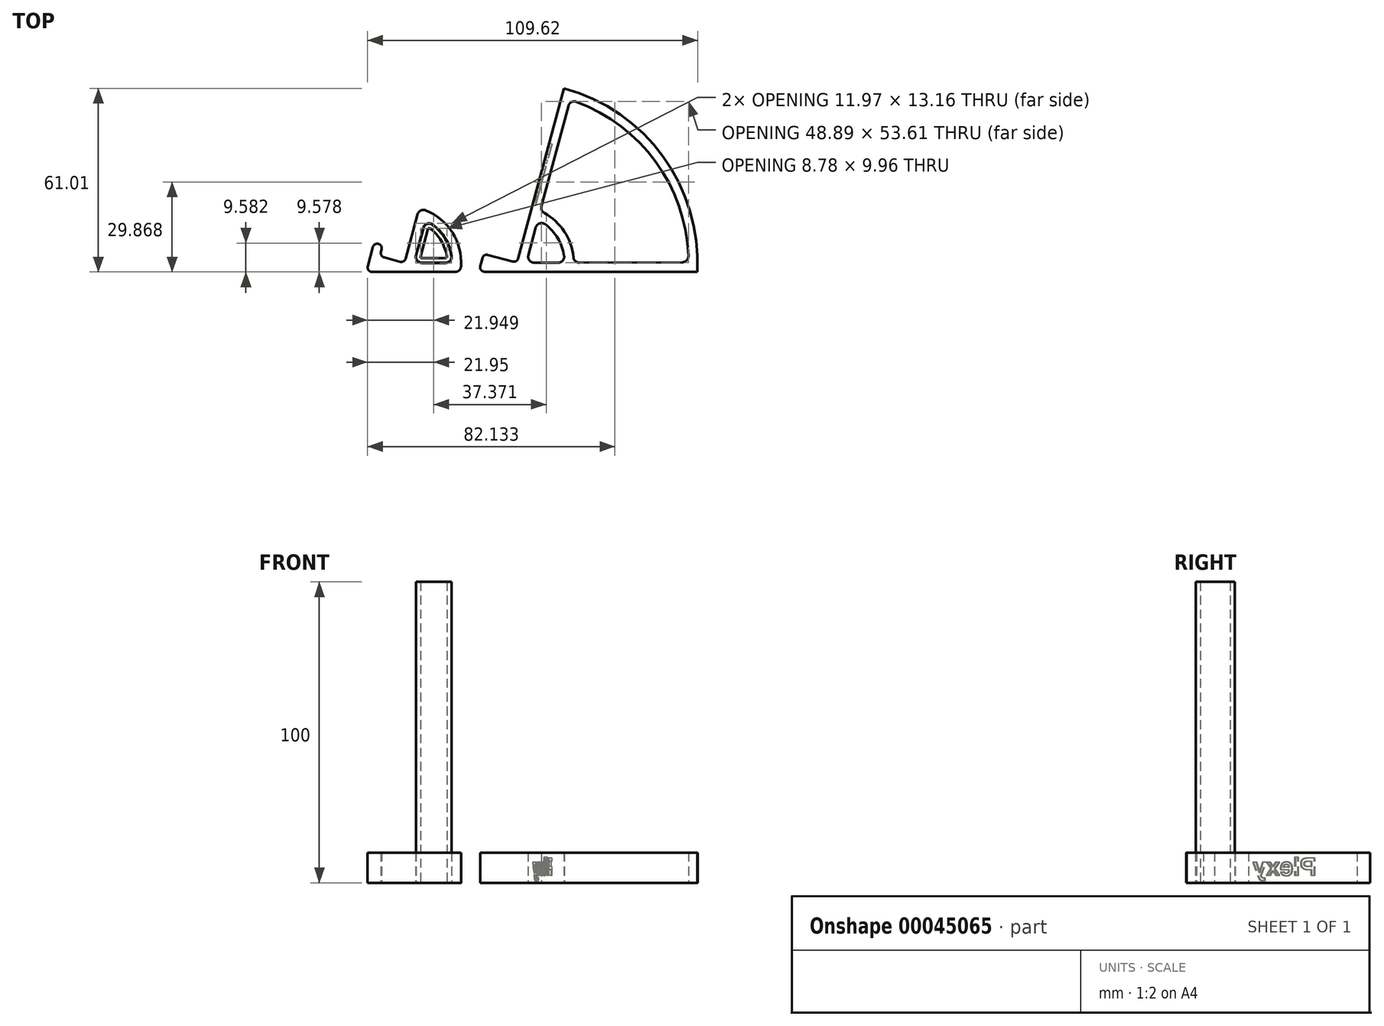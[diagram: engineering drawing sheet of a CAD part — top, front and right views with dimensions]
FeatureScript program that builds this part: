
annotation { "Feature Type Name" : "Feature", "Feature Type Description" : "" }
export const myFeature = defineFeature(function(context is Context, id is Id, definition is map)
    precondition{}
    {
        {
            var Q0;
            Q0=qCreatedBy(makeId("Top.planeOp"),FACE);
            var sketch = newSketch(context, id + "F0", { "sketchPlane" : qUnion([Q0])});
            skArc(sketch, "E0", {"start": v(18.8, 1.88) * mm, "mid": v(15.9, 13.08) * mm, "end": v(7.02, 20.48) * mm});
            skArc(sketch, "E1", {"start": v(15.67, 5.29) * mm, "mid": v(13.56, 11.17) * mm, "end": v(9.35, 15.78) * mm});
            skLineSegment(sketch, "E2", {"start": v(3.78, 5.52) * mm, "end": v(6.24, 14.68) * mm});
            skLineSegment(sketch, "E3", {"start": v(5.71, 3) * mm, "end": v(13.69, 3) * mm});
            skLineSegment(sketch, "E4", {"start": v(16.8, 0) * mm, "end": v(-10.75, 0) * mm});
            skPoint(sketch, "E5.newPointA", {"position": v(5.18, 22.32) * mm});
            skArc(sketch, "E5.filletArc", {"start": v(7.02, 20.48) * mm, "mid": v(5.38, 20.41) * mm, "end": v(4.34, 19.14) * mm});
            skPoint(sketch, "E6.visualSharp", {"position": v(18.6, 0) * mm});
            skArc(sketch, "E6.filletArc", {"start": v(16.8, 0) * mm, "mid": v(18.18, 0.54) * mm, "end": v(18.8, 1.88) * mm});
            skPoint(sketch, "E7.visualSharp", {"position": v(15.83, 3) * mm});
            skArc(sketch, "E7.filletArc", {"start": v(13.69, 3) * mm, "mid": v(15.2, 3.7) * mm, "end": v(15.67, 5.29) * mm});
            skPoint(sketch, "E8.visualSharp", {"position": v(6.92, 17.24) * mm});
            skArc(sketch, "E8.filletArc", {"start": v(9.35, 15.78) * mm, "mid": v(7.5, 16.05) * mm, "end": v(6.24, 14.68) * mm});
            skPoint(sketch, "E9.visualSharp", {"position": v(3.1, 3) * mm});
            skArc(sketch, "E9.filletArc", {"start": v(3.78, 5.52) * mm, "mid": v(4.13, 3.78) * mm, "end": v(5.71, 3) * mm});
            skArc(sketch, "E10.0", {"start": v(3.88, 5.5) * mm, "mid": v(4.2, 3.84) * mm, "end": v(5.71, 3.1) * mm});
            skArc(sketch, "E10.1", {"start": v(9.29, 15.7) * mm, "mid": v(7.54, 15.96) * mm, "end": v(6.33, 14.66) * mm});
            skArc(sketch, "E10.2", {"start": v(15.57, 5.27) * mm, "mid": v(13.48, 11.12) * mm, "end": v(9.29, 15.7) * mm});
            skLineSegment(sketch, "E10.3", {"start": v(3.88, 5.5) * mm, "end": v(6.33, 14.66) * mm});
            skArc(sketch, "E10.4", {"start": v(13.69, 3.1) * mm, "mid": v(15.13, 3.76) * mm, "end": v(15.57, 5.27) * mm});
            skLineSegment(sketch, "E10.5", {"start": v(5.71, 3.1) * mm, "end": v(13.69, 3.1) * mm});
            skLineSegment(sketch, "E11", {"start": v(-7.82, 6.65) * mm, "end": v(-7.6, 7.49) * mm});
            skLineSegment(sketch, "E12", {"start": v(-10.5, 8.26) * mm, "end": v(-12.2, 1.89) * mm});
            skPoint(sketch, "E13.visualSharp", {"position": v(-12.7, 0) * mm});
            skArc(sketch, "E13.filletArc", {"start": v(-12.2, 1.89) * mm, "mid": v(-11.94, 0.59) * mm, "end": v(-10.75, 0) * mm});
            skArc(sketch, "E14", {"start": v(-7.6, 7.49) * mm, "mid": v(-8.66, 9.32) * mm, "end": v(-10.5, 8.26) * mm});
            skPoint(sketch, "E15.visualSharp", {"position": v(-8.21, 5.2) * mm});
            skArc(sketch, "E15.filletArc", {"start": v(-7.82, 6.65) * mm, "mid": v(-7.67, 5.51) * mm, "end": v(-6.76, 4.81) * mm});
            skLineSegment(sketch, "E16", {"start": v(4.34, 19.14) * mm, "end": v(0.39, 4.45) * mm});
            skLineSegment(sketch, "E17", {"start": v(-6.76, 4.81) * mm, "end": v(-1.45, 3.39) * mm});
            skArc(sketch, "E18.filletArc", {"start": v(-1.45, 3.39) * mm, "mid": v(-0.31, 3.54) * mm, "end": v(0.39, 4.45) * mm});
            skArc(sketch, "E19.0", {"start": v(13.69, 4.6) * mm, "mid": v(14, 4.74) * mm, "end": v(14.08, 5.06) * mm});
            skArc(sketch, "E19.1", {"start": v(8.4, 14.49) * mm, "mid": v(8.04, 14.54) * mm, "end": v(7.78, 14.27) * mm});
            skLineSegment(sketch, "E19.2", {"start": v(5.33, 5.1) * mm, "end": v(7.78, 14.27) * mm});
            skArc(sketch, "E19.3", {"start": v(14.08, 5.06) * mm, "mid": v(12.2, 10.34) * mm, "end": v(8.4, 14.49) * mm});
            skArc(sketch, "E19.4", {"start": v(5.33, 5.1) * mm, "mid": v(5.4, 4.76) * mm, "end": v(5.71, 4.6) * mm});
            skLineSegment(sketch, "E19.5", {"start": v(5.71, 4.6) * mm, "end": v(13.69, 4.6) * mm});
            skPoint(sketch, "E20.visualSharp", {"position": v(40.48, 3.06) * mm});
            skPoint(sketch, "E21.visualSharp", {"position": v(29.16, 5.26) * mm});
            skArc(sketch, "E22", {"start": v(56.12, 4.87) * mm, "mid": v(53.11, 13.4) * mm, "end": v(46.47, 19.55) * mm});
            skLineSegment(sketch, "E23", {"start": v(30.6, 4.88) * mm, "end": v(35.92, 3.45) * mm});
            skLineSegment(sketch, "E24", {"start": v(54.18, 0.06) * mm, "end": v(26.62, 0.06) * mm});
            skArc(sketch, "E25", {"start": v(53.04, 5.35) * mm, "mid": v(50.93, 11.23) * mm, "end": v(46.72, 15.84) * mm});
            skPoint(sketch, "E26.visualSharp", {"position": v(24.66, 0.06) * mm});
            skLineSegment(sketch, "E27", {"start": v(41.71, 19.2) * mm, "end": v(37.76, 4.51) * mm});
            skLineSegment(sketch, "E28", {"start": v(41.15, 5.58) * mm, "end": v(43.6, 14.75) * mm});
            skLineSegment(sketch, "E29", {"start": v(43.08, 3.06) * mm, "end": v(51.06, 3.06) * mm});
            skPoint(sketch, "E30.visualSharp", {"position": v(55.96, 0.06) * mm});
            skPoint(sketch, "E31.newPointA", {"position": v(42.55, 22.38) * mm});
            skPoint(sketch, "E32.visualSharp", {"position": v(44.3, 17.3) * mm});
            skLineSegment(sketch, "E33", {"start": v(25.87, 4.6) * mm, "end": v(25.17, 1.95) * mm});
            skPoint(sketch, "E34.visualSharp", {"position": v(53.2, 3.06) * mm});
            skArc(sketch, "E34.filletArc", {"start": v(51.06, 3.06) * mm, "mid": v(52.57, 3.76) * mm, "end": v(53.04, 5.35) * mm});
            skArc(sketch, "E32.filletArc", {"start": v(46.72, 15.84) * mm, "mid": v(44.87, 16.12) * mm, "end": v(43.6, 14.75) * mm});
            skArc(sketch, "E20.filletArc", {"start": v(41.15, 5.58) * mm, "mid": v(41.5, 3.85) * mm, "end": v(43.08, 3.06) * mm});
            skArc(sketch, "E26.filletArc", {"start": v(25.17, 1.95) * mm, "mid": v(25.43, 0.65) * mm, "end": v(26.62, 0.06) * mm});
            skArc(sketch, "E35.filletArc", {"start": v(35.92, 3.45) * mm, "mid": v(37.06, 3.6) * mm, "end": v(37.76, 4.51) * mm});
            skLineSegment(sketch, "E36", {"start": v(41.71, 19.2) * mm, "end": v(52.95, 61) * mm});
            skArc(sketch, "E37", {"start": v(52.95, 61) * mm, "mid": v(85.89, 38.37) * mm, "end": v(97.3, 0.06) * mm});
            skArc(sketch, "E38", {"start": v(57.07, 56.55) * mm, "mid": v(83.47, 36.59) * mm, "end": v(94.33, 5.32) * mm});
            skLineSegment(sketch, "E39", {"start": v(54.18, 0.06) * mm, "end": v(97.3, 0.06) * mm});
            skLineSegment(sketch, "E40.trimOffspring", {"start": v(58.12, 3.06) * mm, "end": v(92.34, 3.24) * mm});
            skLineSegment(sketch, "E41.trimOffspring", {"start": v(45.5, 21.82) * mm, "end": v(54.44, 55.2) * mm});
            skPoint(sketch, "E42.visualSharp", {"position": v(55, 57.27) * mm});
            skArc(sketch, "E42.filletArc", {"start": v(57.07, 56.55) * mm, "mid": v(55.46, 56.45) * mm, "end": v(54.44, 55.2) * mm});
            skPoint(sketch, "E43.visualSharp", {"position": v(45.08, 20.25) * mm});
            skArc(sketch, "E43.filletArc", {"start": v(45.5, 21.82) * mm, "mid": v(45.6, 20.52) * mm, "end": v(46.47, 19.55) * mm});
            skPoint(sketch, "E44.visualSharp", {"position": v(56.2, 3.05) * mm});
            skArc(sketch, "E44.filletArc", {"start": v(56.12, 4.87) * mm, "mid": v(56.77, 3.58) * mm, "end": v(58.12, 3.06) * mm});
            skPoint(sketch, "E45.visualSharp", {"position": v(94.37, 3.25) * mm});
            skArc(sketch, "E45.filletArc", {"start": v(92.34, 3.24) * mm, "mid": v(93.77, 3.86) * mm, "end": v(94.33, 5.32) * mm});
            skLineSegment(sketch, "E46", {"start": v(30.6, 4.88) * mm, "end": v(27.71, 5.65) * mm});
            skPoint(sketch, "E47.visualSharp", {"position": v(26.26, 6.04) * mm});
            skArc(sketch, "E47.filletArc", {"start": v(27.71, 5.65) * mm, "mid": v(26.57, 5.5) * mm, "end": v(25.87, 4.6) * mm});
            skLineSegment(sketch, "E48", {"start": v(-6.76, 4.81) * mm, "end": v(-14.99, 7.02) * mm, "construction": true});
            skSolve(sketch);
        }
        {
            var Q0;
            Q0=makeQuery(id+"F0.imprint","IMPRINT",FACE,{"disambiguationData":[TD([[makeQuery(id+"F0.imprint","IMPRINT",EDGE,{"derivedFrom":sQuery(id+"F0.wireOp",EDGE,"E10.0")}),1.0]])]});
            extrude(context, id + "F1", {"entities" : qUnion([Q0]), "depth" : 100 * mm});
        }
        {
            var Q0;
            Q0=makeQuery(id+"F0.imprint","IMPRINT",FACE,{"disambiguationData":[TD([[makeQuery(id+"F0.imprint","IMPRINT",EDGE,{"derivedFrom":sQuery(id+"F0.wireOp",EDGE,"E0")}),1.0]])]});
            extrude(context, id + "F2", {"entities" : qUnion([Q0]), "depth" : 10 * mm});
        }
        {
            var Q0;
            Q0=makeQuery(id+"F0.imprint","IMPRINT",FACE,{"disambiguationData":[TD([[makeQuery(id+"F0.imprint","IMPRINT",EDGE,{"derivedFrom":sQuery(id+"F0.wireOp",EDGE,"E22")}),1.0]])]});
            extrude(context, id + "F3", {"entities" : qUnion([Q0]), "depth" : 10 * mm});
        }
        {
            var Q0;
            Q0=makeQuery(id+"F3.opExtrude","SWEPT_FACE",FACE,{"disambiguationData":[OSD([sQuery(id+"F0.wireOp",EDGE,"E27"),sQuery(id+"F0.wireOp",EDGE,"E36")])]});
            var sketch = newSketch(context, id + "F4", { "sketchPlane" : qUnion([Q0])});
            skText(sketch, "E49", { "text": "Plexy", "fontName": "Arimo-Bold.ttf"});
            skPoint(sketch, "E50", {"position": v(-43.41, 10) * mm});
            const initialGuessF4  = {"E49": [-0.05428, 0.00243, 1, 0, 0.006]};
            skSetInitialGuess(sketch, initialGuessF4);
            skSolve(sketch);
        }
        {
            var Q0;
            Q0=makeQuery(id+"F4.imprint","IMPRINT",FACE,{"disambiguationData":[TD([[makeQuery(id+"F4.imprint","IMPRINT",EDGE,{"derivedFrom":sQuery(id+"F4.wireOp",EDGE,"E49.sketch_text.stroke-50")}),-1.0]])]});
            var Q1;
            Q1=makeQuery(id+"F4.imprint","IMPRINT",FACE,{"disambiguationData":[TD([[makeQuery(id+"F4.imprint","IMPRINT",EDGE,{"derivedFrom":sQuery(id+"F4.wireOp",EDGE,"E49.sketch_text.stroke-38")}),-1.0]])]});
            var Q2;
            Q2=makeQuery(id+"F4.imprint","IMPRINT",FACE,{"disambiguationData":[TD([[makeQuery(id+"F4.imprint","IMPRINT",EDGE,{"derivedFrom":sQuery(id+"F4.wireOp",EDGE,"E49.sketch_text.stroke-20")}),-1.0]])]});
            var Q3;
            Q3=makeQuery(id+"F4.imprint","IMPRINT",FACE,{"disambiguationData":[TD([[makeQuery(id+"F4.imprint","IMPRINT",EDGE,{"derivedFrom":sQuery(id+"F4.wireOp",EDGE,"E49.sketch_text.stroke-0")}),-1.0]])]});
            var Q4;
            Q4=makeQuery(id+"F4.imprint","IMPRINT",FACE,{"disambiguationData":[TD([[makeQuery(id+"F4.imprint","IMPRINT",EDGE,{"derivedFrom":sQuery(id+"F4.wireOp",EDGE,"E49.sketch_text.stroke-16")}),-1.0]])]});
            extrude(context, id + "F5", {"entities" : qUnion([Q0, Q1, Q2, Q3, Q4]), "operationType" : NewBodyOperationType.REMOVE, "oppositeDirection" : true, "depth" : 1 * mm});
        }
    });
